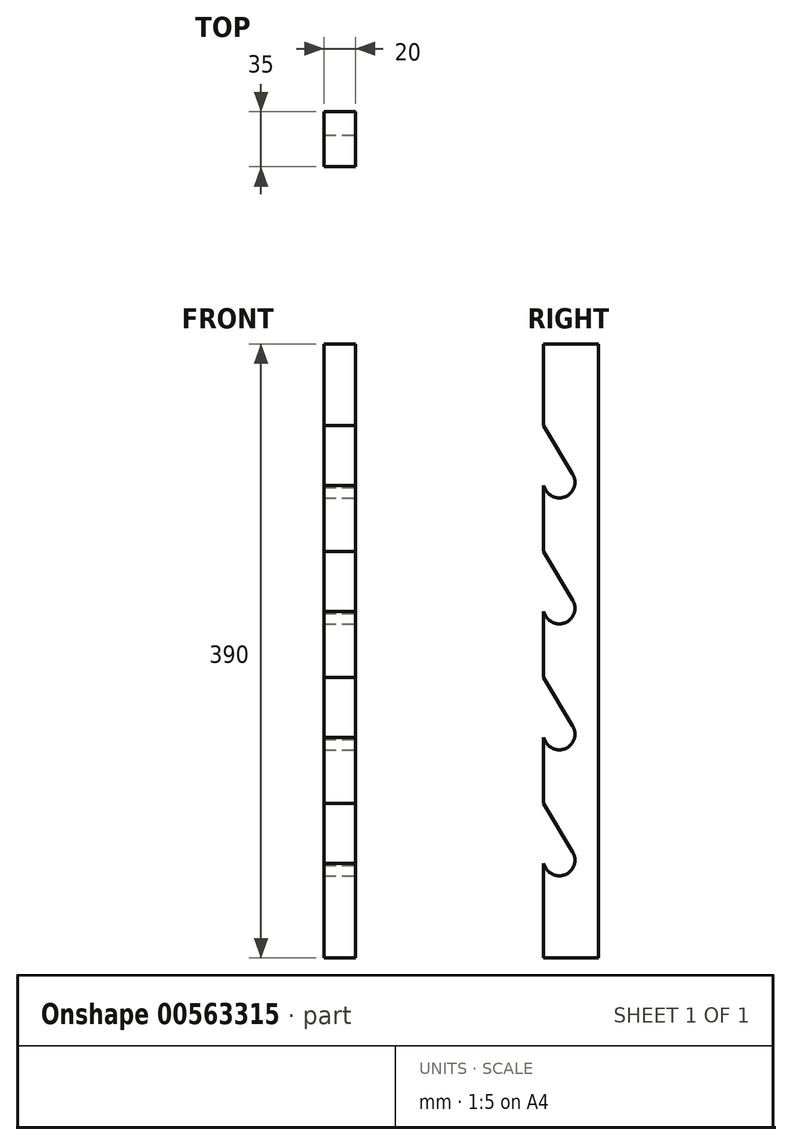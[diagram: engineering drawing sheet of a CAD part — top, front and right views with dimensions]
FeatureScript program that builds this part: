
annotation { "Feature Type Name" : "Feature", "Feature Type Description" : "" }
export const myFeature = defineFeature(function(context is Context, id is Id, definition is map)
    precondition{}
    {
        {
            var Q0;
            Q0=qCreatedBy(makeId("Right.planeOp"),FACE);
            var sketch = newSketch(context, id + "F0", { "sketchPlane" : qUnion([Q0])});
            skLineSegment(sketch, "E0.bottom", {"start": v(-65.52, 319.1) * mm, "end": v(-15.52, 319.1) * mm});
            skLineSegment(sketch, "E0.top", {"start": v(-65.52, -70.9) * mm, "end": v(-15.52, -70.9) * mm});
            skLineSegment(sketch, "E0.left", {"start": v(-65.52, 319.1) * mm, "end": v(-65.52, -70.9) * mm});
            skLineSegment(sketch, "E0.right", {"start": v(-15.52, 319.1) * mm, "end": v(-15.52, -70.9) * mm});
            skSolve(sketch);
        }
        {
            var Q0;
            Q0=qSketchRegion(id+"F0",true);
            extrude(context, id + "F1", {"entities" : qUnion([Q0]), "depth" : 20 * mm, "offsetDistance" : 25 * mm});
        }
        {
            var Q0;
            Q0=makeQuery(id+"F1.opExtrude","CAP_FACE",FACE,{"disambiguationData":[OSD([sQuery(id+"F0.wireOp",EDGE,"E0.bottom"),sQuery(id+"F0.wireOp",EDGE,"E0.top"),sQuery(id+"F0.wireOp",EDGE,"E0.left"),sQuery(id+"F0.wireOp",EDGE,"E0.right")])],"isStart":false});
            var sketch = newSketch(context, id + "F2", { "sketchPlane" : qUnion([Q0])});
            skLineSegment(sketch, "E1", {"start": v(-65.52, 51.74) * mm, "end": v(-31.84, -3.56) * mm});
            skLineSegment(sketch, "E2", {"start": v(-65.52, 13.7) * mm, "end": v(-49.81, -12.09) * mm});
            skLineSegment(sketch, "E3", {"start": v(-65.52, 51.74) * mm, "end": v(-65.52, 13.7) * mm});
            skArc(sketch, "E4", {"start": v(-31.84, -3.56) * mm, "mid": v(-36.1, -17.8) * mm, "end": v(-49.81, -12.09) * mm});
            skLineSegment(sketch, "E5.0.1.0", {"start": v(-65.52, 131.74) * mm, "end": v(-65.52, 93.7) * mm});
            skLineSegment(sketch, "E5.0.1.1", {"start": v(-65.52, 131.74) * mm, "end": v(-31.84, 76.44) * mm});
            skArc(sketch, "E5.0.1.2", {"start": v(-31.84, 76.44) * mm, "mid": v(-36.1, 62.2) * mm, "end": v(-49.81, 67.91) * mm});
            skLineSegment(sketch, "E5.0.1.3", {"start": v(-65.52, 93.7) * mm, "end": v(-49.81, 67.91) * mm});
            skLineSegment(sketch, "E5.0.2.0", {"start": v(-65.52, 211.74) * mm, "end": v(-65.52, 173.7) * mm});
            skLineSegment(sketch, "E5.0.2.1", {"start": v(-65.52, 211.74) * mm, "end": v(-31.84, 156.44) * mm});
            skArc(sketch, "E5.0.2.2", {"start": v(-31.84, 156.44) * mm, "mid": v(-36.1, 142.2) * mm, "end": v(-49.81, 147.91) * mm});
            skLineSegment(sketch, "E5.0.2.3", {"start": v(-65.52, 173.7) * mm, "end": v(-49.81, 147.91) * mm});
            skLineSegment(sketch, "E5.0.3.0", {"start": v(-65.52, 291.74) * mm, "end": v(-65.52, 253.7) * mm});
            skLineSegment(sketch, "E5.0.3.1", {"start": v(-65.52, 291.74) * mm, "end": v(-31.84, 236.44) * mm});
            skArc(sketch, "E5.0.3.2", {"start": v(-31.84, 236.44) * mm, "mid": v(-36.1, 222.2) * mm, "end": v(-49.81, 227.91) * mm});
            skLineSegment(sketch, "E5.0.3.3", {"start": v(-65.52, 253.7) * mm, "end": v(-49.81, 227.91) * mm});
            skLineSegment(sketch, "E5.direction1", {"start": v(-65.52, 13.7) * mm, "end": v(-40.52, 13.7) * mm, "construction": true});
            skLineSegment(sketch, "E5.direction2", {"start": v(-65.52, 13.7) * mm, "end": v(-65.52, 93.7) * mm, "construction": true});
            skSolve(sketch);
        }
        {
            var Q0;
            Q0=qSketchRegion(id+"F2",true);
            extrude(context, id + "F3", {"entities" : qUnion([Q0]), "operationType" : NewBodyOperationType.REMOVE, "endBound" : BoundingType.THROUGH_ALL, "oppositeDirection" : true, "depth" : 25 * mm, "offsetDistance" : 25 * mm});
        }
        {
            var Q0;
            Q0=makeQuery(id+"F1.opExtrude","CAP_FACE",FACE,{"disambiguationData":[OSD([sQuery(id+"F0.wireOp",EDGE,"E0.bottom"),sQuery(id+"F0.wireOp",EDGE,"E0.top"),sQuery(id+"F0.wireOp",EDGE,"E0.left"),sQuery(id+"F0.wireOp",EDGE,"E0.right")])],"isStart":false});
            var sketch = newSketch(context, id + "F4", { "sketchPlane" : qUnion([Q0])});
            skLineSegment(sketch, "E6.bottom", {"start": v(-65.52, -70.9) * mm, "end": v(-50.52, -70.9) * mm});
            skLineSegment(sketch, "E6.top", {"start": v(-65.52, 319.1) * mm, "end": v(-50.52, 319.1) * mm});
            skLineSegment(sketch, "E6.left", {"start": v(-65.52, -70.9) * mm, "end": v(-65.52, 319.1) * mm});
            skLineSegment(sketch, "E6.right", {"start": v(-50.52, -70.9) * mm, "end": v(-50.52, 319.1) * mm});
            skSolve(sketch);
        }
        {
            var Q0;
            Q0 = qSketchRegion(id + "F4", true);
            extrude(context, id + "F5", {"entities" : qUnion([Q0]), "operationType" : NewBodyOperationType.REMOVE, "endBound" : BoundingType.THROUGH_ALL, "oppositeDirection" : true, "depth" : 25 * mm, "offsetDistance" : 25 * mm});
        }
    });
